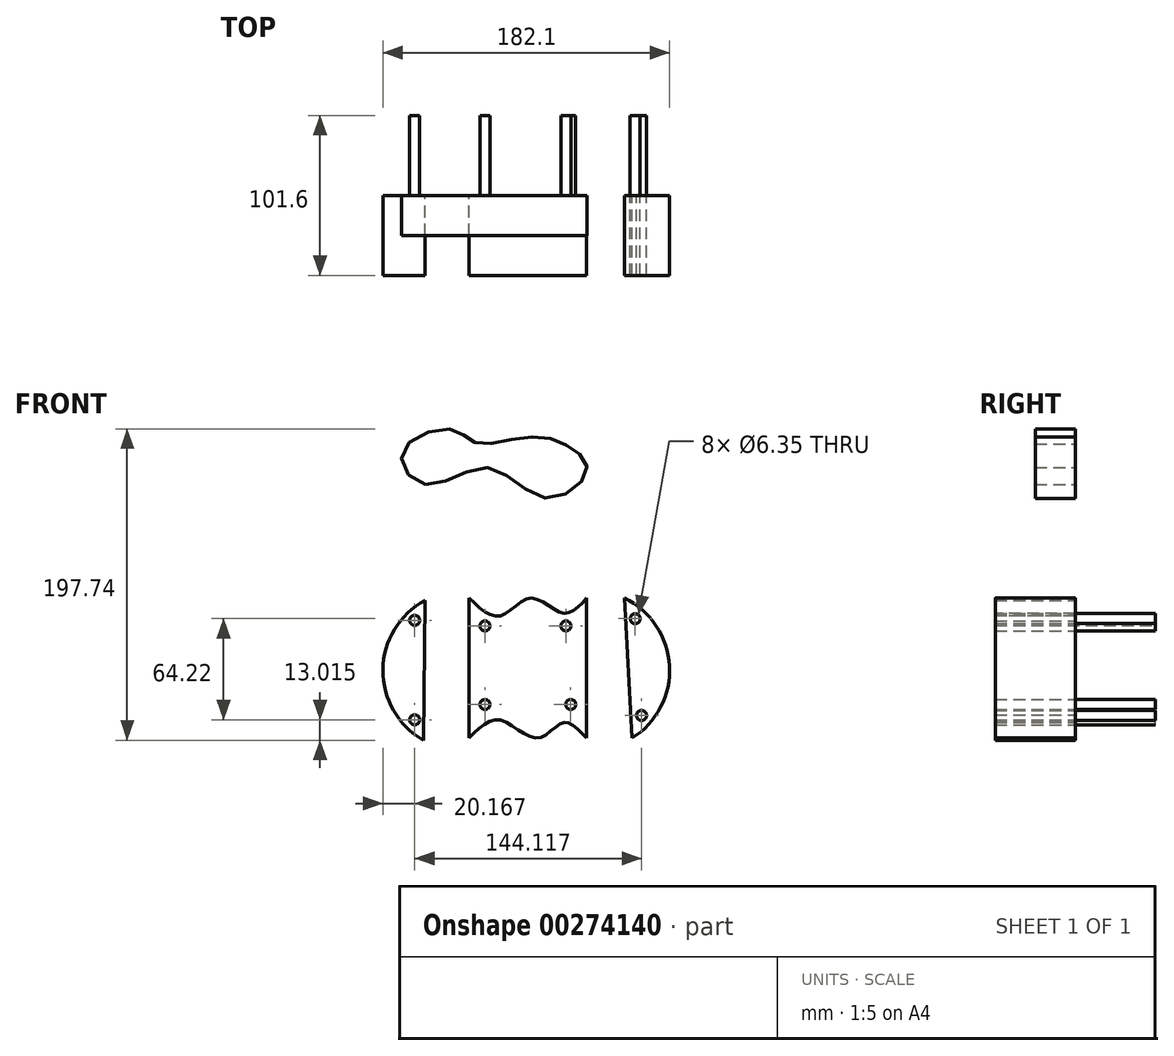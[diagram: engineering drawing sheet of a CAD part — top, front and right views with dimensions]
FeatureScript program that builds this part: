
annotation { "Feature Type Name" : "Feature", "Feature Type Description" : "" }
export const myFeature = defineFeature(function(context is Context, id is Id, definition is map)
    precondition{}
    {
        {
            var Q0;
            Q0=qCreatedBy(makeId("Front.planeOp"),FACE);
            var sketch = newSketch(context, id + "F0", { "sketchPlane" : qUnion([Q0])});
            skArc(sketch, "E0", {"start": v(-55.22, 39.23) * mm, "mid": v(-81.91, -4.93) * mm, "end": v(-56.2, -49.66) * mm});
            skLineSegment(sketch, "E1", {"start": v(-55.22, 39.23) * mm, "end": v(-56.2, -49.66) * mm});
            skLineSegment(sketch, "E2", {"start": v(-27.13, 40.64) * mm, "end": v(-27.13, -48.26) * mm});
            skFitSpline(sketch, "E3", {"points": [v(-27.13, 40.64) * mm, v(-7.42, 29.41) * mm, v(12, 40.64) * mm, v(32.56, 31.13) * mm, v(47.4, 40.64) * mm], "startDerivative": vector(77.12, -74.22) * mm, "endDerivative": vector(61.33, 68.55) * mm});
            skLineSegment(sketch, "E4", {"start": v(47.4, 40.64) * mm, "end": v(47.4, -48.26) * mm});
            skFitSpline(sketch, "E5", {"points": [v(-27.13, -48.26) * mm, v(-7.42, -36.84) * mm, v(16, -48.26) * mm, v(32.56, -38.55) * mm, v(47.4, -48.26) * mm], "startDerivative": vector(73.03, 74.25) * mm, "endDerivative": vector(65, -71.2) * mm});
            skFitSpline(sketch, "E6", {"points": [v(-101.14, -6.09) * mm, v(-105.92, -5.48) * mm, v(-106.2, -5.44) * mm], "startDerivative": vector(-7.74, 0.99) * mm, "endDerivative": vector(-1, 0.13) * mm});
            skArc(sketch, "E7", {"start": v(76.25, -48.26) * mm, "mid": v(100.1, -2.38) * mm, "end": v(71.4, 40.64) * mm});
            skLineSegment(sketch, "E8", {"start": v(71.4, 40.64) * mm, "end": v(76.25, -48.26) * mm});
            skCircle(sketch, "E9", {"center": v(-61.75, 26.54) * mm, "radius": 3.18 * mm});
            skCircle(sketch, "E10", {"center": v(-61.75, -36.64) * mm, "radius": 3.18 * mm});
            skCircle(sketch, "E11", {"center": v(-17.13, 23) * mm, "radius": 3.18 * mm});
            skCircle(sketch, "E12", {"center": v(-17.13, -26.91) * mm, "radius": 3.18 * mm});
            skCircle(sketch, "E13", {"center": v(34.3, 23) * mm, "radius": 3.18 * mm});
            skCircle(sketch, "E14", {"center": v(37.36, -26.91) * mm, "radius": 3.18 * mm});
            skCircle(sketch, "E15", {"center": v(78.29, 27.58) * mm, "radius": 3.18 * mm});
            skCircle(sketch, "E16", {"center": v(82.36, -33.9) * mm, "radius": 3.18 * mm});
            skSolve(sketch);
        }
        {
            var Q0;
            Q0 = qSketchRegion(id + "F0", true);
            extrude(context, id + "F1", {"entities" : qUnion([Q0]), "depth" : 50.8 * mm});
        }
        {
            var Q0;
            Q0=makeQuery(id+"F0.imprint","IMPRINT",FACE,{"disambiguationData":[TD([[makeQuery(id+"F0.imprint","IMPRINT",EDGE,{"derivedFrom":sQuery(id+"F0.wireOp",EDGE,"E9")}),1.0]])]});
            var Q1;
            Q1=makeQuery(id+"F0.imprint","IMPRINT",FACE,{"disambiguationData":[TD([[makeQuery(id+"F0.imprint","IMPRINT",EDGE,{"derivedFrom":sQuery(id+"F0.wireOp",EDGE,"E10")}),1.0]])]});
            var Q2;
            Q2=makeQuery(id+"F0.imprint","IMPRINT",FACE,{"disambiguationData":[TD([[makeQuery(id+"F0.imprint","IMPRINT",EDGE,{"derivedFrom":sQuery(id+"F0.wireOp",EDGE,"E14")}),1.0]])]});
            var Q3;
            Q3=makeQuery(id+"F0.imprint","IMPRINT",FACE,{"disambiguationData":[TD([[makeQuery(id+"F0.imprint","IMPRINT",EDGE,{"derivedFrom":sQuery(id+"F0.wireOp",EDGE,"E13")}),1.0]])]});
            var Q4;
            Q4=makeQuery(id+"F0.imprint","IMPRINT",FACE,{"disambiguationData":[TD([[makeQuery(id+"F0.imprint","IMPRINT",EDGE,{"derivedFrom":sQuery(id+"F0.wireOp",EDGE,"E15")}),1.0]])]});
            var Q5;
            Q5=makeQuery(id+"F0.imprint","IMPRINT",FACE,{"disambiguationData":[TD([[makeQuery(id+"F0.imprint","IMPRINT",EDGE,{"derivedFrom":sQuery(id+"F0.wireOp",EDGE,"E12")}),1.0]])]});
            var Q6;
            Q6=makeQuery(id+"F0.imprint","IMPRINT",FACE,{"disambiguationData":[TD([[makeQuery(id+"F0.imprint","IMPRINT",EDGE,{"derivedFrom":sQuery(id+"F0.wireOp",EDGE,"E11")}),1.0]])]});
            var Q7;
            Q7=makeQuery(id+"F0.imprint","IMPRINT",FACE,{"disambiguationData":[TD([[makeQuery(id+"F0.imprint","IMPRINT",EDGE,{"derivedFrom":sQuery(id+"F0.wireOp",EDGE,"E16")}),1.0]])]});
            extrude(context, id + "F2", {"entities" : qUnion([Q0, Q1, Q2, Q3, Q4, Q5, Q6, Q7]), "endBound" : BoundingType.SYMMETRIC, "depth" : 101.6 * mm});
        }
        {
            var Q0;
            Q0=qCreatedBy(makeId("Front.planeOp"),FACE);
            var sketch = newSketch(context, id + "F3", { "sketchPlane" : qUnion([Q0])});
            skFitSpline(sketch, "E17", {"points": [v(-55.01, 112.84) * mm, v(-15.42, 123.53) * mm, v(21.89, 104.1) * mm, v(47.58, 121.52) * mm, v(37.23, 136.4) * mm, v(11.24, 142.99) * mm, v(-22.5, 139.19) * mm, v(-38.4, 147.77) * mm, v(-69.58, 133.51) * mm, v(-55.01, 112.84) * mm]});
            skSolve(sketch);
        }
        {
            var Q0;
            Q0 = qSketchRegion(id + "F3", true);
            extrude(context, id + "F4", {"entities" : qUnion([Q0]), "depth" : 25.4 * mm});
        }
    });
